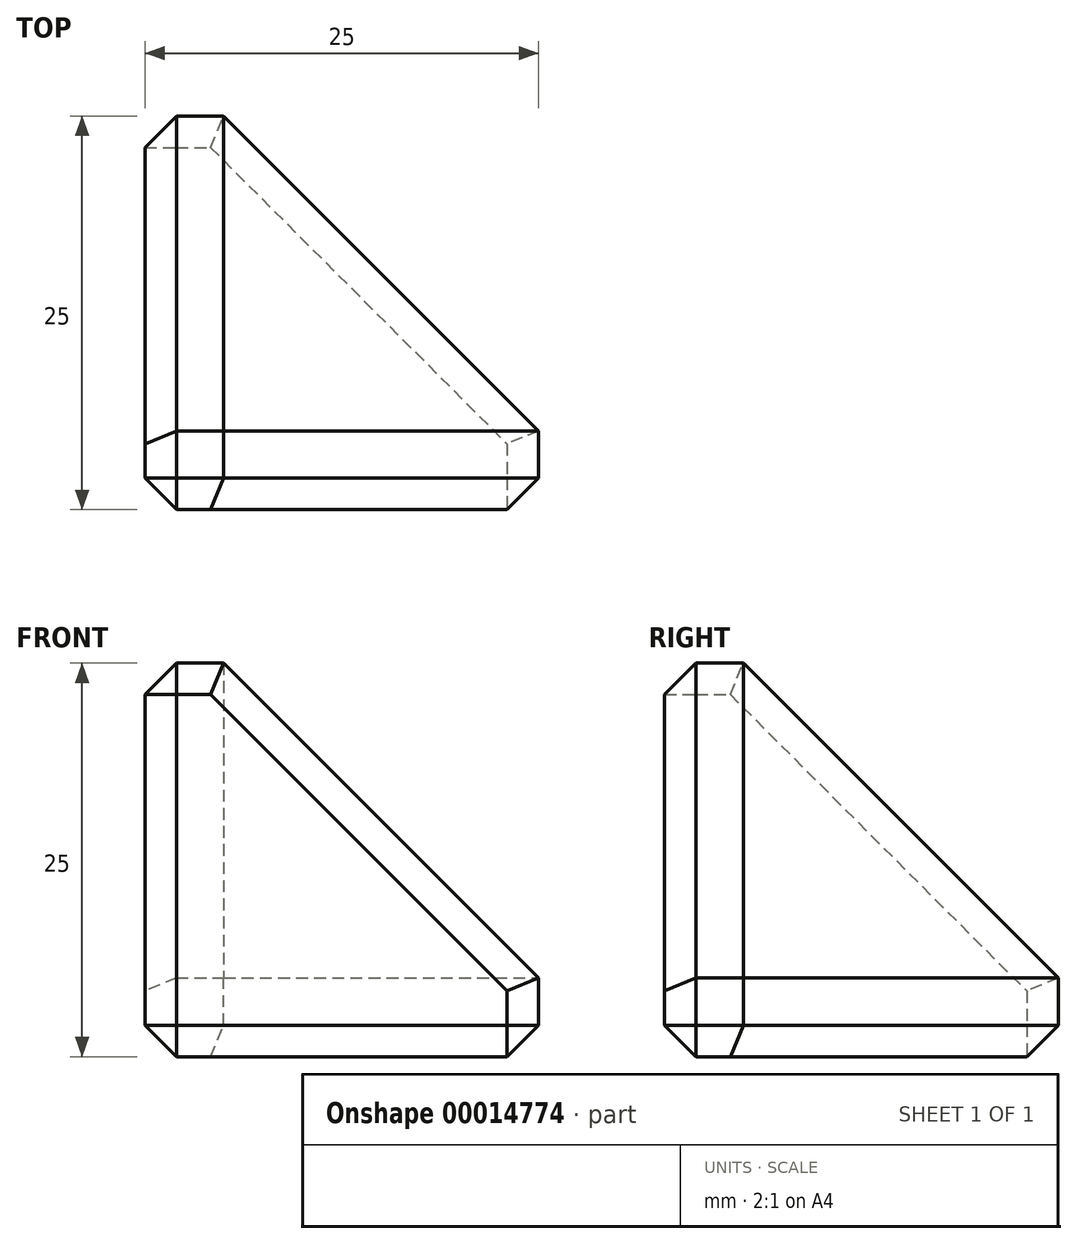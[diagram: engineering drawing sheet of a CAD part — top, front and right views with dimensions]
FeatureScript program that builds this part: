
annotation { "Feature Type Name" : "Feature", "Feature Type Description" : "" }
export const myFeature = defineFeature(function(context is Context, id is Id, definition is map)
    precondition{}
    {
        {
            var Q0;
            Q0=qCreatedBy(makeId("Top.planeOp"),FACE);
            var sketch = newSketch(context, id + "F0", { "sketchPlane" : qUnion([Q0])});
            skLineSegment(sketch, "E0.bottom", {"start": v(-12.87, 14.16) * mm, "end": v(12.13, 14.16) * mm});
            skLineSegment(sketch, "E0.top", {"start": v(-12.87, -10.84) * mm, "end": v(12.13, -10.84) * mm});
            skLineSegment(sketch, "E0.left", {"start": v(-12.87, 14.16) * mm, "end": v(-12.87, -10.84) * mm});
            skLineSegment(sketch, "E0.right", {"start": v(12.13, 14.16) * mm, "end": v(12.13, -10.84) * mm});
            skSolve(sketch);
        }
        {
            var Q0;
            Q0=makeQuery(id+"F0.imprint","IMPRINT",FACE,{"disambiguationData":[TD([[makeQuery(id+"F0.imprint","IMPRINT",EDGE,{"derivedFrom":sQuery(id+"F0.wireOp",EDGE,"E0.bottom")}),-1.0]])]});
            extrude(context, id + "F1", {"entities" : qUnion([Q0]), "depth" : 25 * mm});
        }
        {
            var Q0;
            Q0=makeQuery(id+"F1.opExtrude","CAP_FACE",FACE,{"disambiguationData":[OSD([sQuery(id+"F0.wireOp",EDGE,"E0.bottom"),sQuery(id+"F0.wireOp",EDGE,"E0.top"),sQuery(id+"F0.wireOp",EDGE,"E0.left"),sQuery(id+"F0.wireOp",EDGE,"E0.right")])],"isStart":false});
            var sketch = newSketch(context, id + "F2", { "sketchPlane" : qUnion([Q0])});
            skLineSegment(sketch, "E1", {"start": v(-7.87, 14.16) * mm, "end": v(-7.87, -5.84) * mm});
            skLineSegment(sketch, "E2", {"start": v(-7.87, -5.84) * mm, "end": v(12.13, -5.84) * mm});
            skLineSegment(sketch, "E3", {"start": v(12.13, -5.84) * mm, "end": v(12.13, 14.16) * mm});
            skLineSegment(sketch, "E4", {"start": v(12.13, 14.16) * mm, "end": v(-7.87, 14.16) * mm});
            skSolve(sketch);
        }
        {
            var Q0;
            Q0=makeQuery(id+"F2.imprint","IMPRINT",FACE,{"disambiguationData":[TD([[makeQuery(id+"F2.imprint","IMPRINT",EDGE,{"derivedFrom":sQuery(id+"F2.wireOp",EDGE,"E1")}),1.0]])]});
            extrude(context, id + "F3", {"entities" : qUnion([Q0]), "operationType" : NewBodyOperationType.REMOVE, "oppositeDirection" : true, "depth" : 20 * mm});
        }
        {
            var Q0;
            Q0=makeQuery(id+"F1.opExtrude","SWEPT_EDGE",EDGE,{"disambiguationData":[OSD([sQuery(id+"F0.wireOp",EDGE,"E0.top"),sQuery(id+"F0.wireOp",EDGE,"E0.left")])]});
            var Q1;
            Q1=makeQuery(id+"F1.opExtrude","CAP_EDGE",EDGE,{"disambiguationData":[OSD([sQuery(id+"F0.wireOp",EDGE,"E0.left")])],"isStart":false});
            var Q2;
            Q2=makeQuery(id+"F1.opExtrude","CAP_EDGE",EDGE,{"disambiguationData":[OSD([sQuery(id+"F0.wireOp",EDGE,"E0.top")])],"isStart":false});
            var Q3;
            Q3=makeQuery(id+"F1.opExtrude","SWEPT_EDGE",EDGE,{"disambiguationData":[OSD([sQuery(id+"F0.wireOp",EDGE,"E0.top"),sQuery(id+"F0.wireOp",EDGE,"E0.right")])]});
            var Q4;
            Q4=makeQuery(id+"F1.opExtrude","CAP_EDGE",EDGE,{"disambiguationData":[OSD([sQuery(id+"F0.wireOp",EDGE,"E0.top")])],"isStart":true});
            var Q5;
            Q5=makeQuery(id+"F1.opExtrude","CAP_EDGE",EDGE,{"disambiguationData":[OSD([sQuery(id+"F0.wireOp",EDGE,"E0.right")])],"isStart":true});
            var Q6;
            Q6=makeQuery(id+"F1.opExtrude","CAP_EDGE",EDGE,{"disambiguationData":[OSD([sQuery(id+"F0.wireOp",EDGE,"E0.bottom")])],"isStart":true});
            var Q7;
            Q7=makeQuery(id+"F1.opExtrude","SWEPT_EDGE",EDGE,{"disambiguationData":[OSD([sQuery(id+"F0.wireOp",EDGE,"E0.bottom"),sQuery(id+"F0.wireOp",EDGE,"E0.left")])]});
            var Q8;
            Q8=makeQuery(id+"F1.opExtrude","CAP_EDGE",EDGE,{"disambiguationData":[OSD([sQuery(id+"F0.wireOp",EDGE,"E0.left")])],"isStart":true});
            var Q9;
            Q9=makeQuery(id+"F1.opExtrude","CAP_EDGE",EDGE,{"disambiguationData":[OSD([sQuery(id+"F0.wireOp",EDGE,"E0.right")])],"isStart":false});
            var Q10;
            Q10=makeQuery(id+"F1.opExtrude","SWEPT_EDGE",EDGE,{"disambiguationData":[OSD([sQuery(id+"F0.wireOp",EDGE,"E0.bottom"),sQuery(id+"F0.wireOp",EDGE,"E0.right")])]});
            var Q11;
            Q11=makeQuery(id+"F1.opExtrude","CAP_EDGE",EDGE,{"disambiguationData":[OSD([sQuery(id+"F0.wireOp",EDGE,"E0.bottom")])],"isStart":false});
            chamfer(context, id + "F4", {"entities" : qUnion([Q0, Q1, Q2, Q3, Q4, Q5, Q6, Q7, Q8, Q9, Q10, Q11]), "width" : 2 * mm, "tangentPropagation" : true});
        }
        {
            var Q0;
            Q0=makeQuery(id+"F3.boolean.opBoolean","COPY",FACE,{"derivedFrom":makeQuery(id+"F3.opExtrude","SWEPT_FACE",FACE,{"disambiguationData":[OSD([sQuery(id+"F2.wireOp",EDGE,"E2")])]})});
            var sketch = newSketch(context, id + "F5", { "sketchPlane" : qUnion([Q0])});
            skLineSegment(sketch, "E5", {"start": v(-12.13, 5) * mm, "end": v(7.87, 25) * mm});
            skLineSegment(sketch, "E6", {"start": v(7.87, 25) * mm, "end": v(-12.13, 25) * mm});
            skLineSegment(sketch, "E7", {"start": v(-12.13, 25) * mm, "end": v(-12.13, 5) * mm});
            skSolve(sketch);
        }
        {
            var Q0;
            {var subQ0=sQuery(id+"F5.wireOp",EDGE,"E5");Q0=makeQuery(id+"F5.imprint","IMPRINT",FACE,{"disambiguationData":[TD([[makeQuery(id+"F5.imprint","IMPRINT",EDGE,{"derivedFrom":subQ0}),1.0]])]});}
            extrude(context, id + "F6", {"entities" : qUnion([Q0]), "operationType" : NewBodyOperationType.REMOVE, "oppositeDirection" : true, "depth" : 25 * mm});
        }
        {
            var Q0;
            Q0=makeQuery(id+"F3.boolean.opBoolean","COPY",FACE,{"derivedFrom":makeQuery(id+"F3.opExtrude","SWEPT_FACE",FACE,{"disambiguationData":[OSD([sQuery(id+"F2.wireOp",EDGE,"E1")])]})});
            var sketch = newSketch(context, id + "F7", { "sketchPlane" : qUnion([Q0])});
            skLineSegment(sketch, "E8", {"start": v(-5.84, 25) * mm, "end": v(14.16, 5) * mm});
            skLineSegment(sketch, "E9", {"start": v(14.16, 5) * mm, "end": v(14.16, 25) * mm});
            skPoint(sketch, "E9.endSnap0", {"position": v(14.16, 14) * mm});
            skLineSegment(sketch, "E10", {"start": v(14.16, 25) * mm, "end": v(-5.84, 25) * mm});
            skSolve(sketch);
        }
        {
            var Q0;
            {var subQ0=sQuery(id+"F7.wireOp",EDGE,"E8");Q0=makeQuery(id+"F7.imprint","IMPRINT",FACE,{"disambiguationData":[TD([[makeQuery(id+"F7.imprint","IMPRINT",EDGE,{"derivedFrom":subQ0}),1.0]])]});}
            extrude(context, id + "F8", {"entities" : qUnion([Q0]), "operationType" : NewBodyOperationType.REMOVE, "oppositeDirection" : true, "depth" : 25 * mm});
        }
        {
            var Q0;
            Q0=makeQuery(id+"F3.boolean.opBoolean","COPY",FACE,{"derivedFrom":makeQuery(id+"F3.opExtrude","CAP_FACE",FACE,{"disambiguationData":[OSD([sQuery(id+"F2.wireOp",EDGE,"E1"),sQuery(id+"F2.wireOp",EDGE,"E2"),sQuery(id+"F2.wireOp",EDGE,"E3"),sQuery(id+"F2.wireOp",EDGE,"E4")])],"isStart":false})});
            var sketch = newSketch(context, id + "F9", { "sketchPlane" : qUnion([Q0])});
            skLineSegment(sketch, "E11", {"start": v(-7.87, 14.16) * mm, "end": v(12.13, -5.84) * mm});
            skLineSegment(sketch, "E12", {"start": v(12.13, -5.84) * mm, "end": v(12.13, 14.16) * mm});
            skLineSegment(sketch, "E13", {"start": v(12.13, 14.16) * mm, "end": v(-7.87, 14.16) * mm});
            skSolve(sketch);
        }
        {
            var Q0;
            {var subQ0=sQuery(id+"F9.wireOp",EDGE,"E11");Q0=makeQuery(id+"F9.imprint","IMPRINT",FACE,{"disambiguationData":[TD([[makeQuery(id+"F9.imprint","IMPRINT",EDGE,{"derivedFrom":subQ0}),1.0]])]});}
            extrude(context, id + "F10", {"entities" : qUnion([Q0]), "operationType" : NewBodyOperationType.REMOVE, "oppositeDirection" : true, "depth" : 25 * mm});
        }
        {
            var Q0;
            Q0=makeQuery(id+"F10.boolean.opBoolean","INTERSECT",EDGE,{"derivedFrom":[makeQuery(id+"F1.opExtrude","CAP_FACE",FACE,{"disambiguationData":[OSD([sQuery(id+"F0.wireOp",EDGE,"E0.bottom"),sQuery(id+"F0.wireOp",EDGE,"E0.top"),sQuery(id+"F0.wireOp",EDGE,"E0.left"),sQuery(id+"F0.wireOp",EDGE,"E0.right")])],"isStart":true}),makeQuery(id+"F10.opExtrude","SWEPT_FACE",FACE,{"disambiguationData":[OSD([sQuery(id+"F9.wireOp",EDGE,"E11")])]})]});
            var Q1;
            Q1=makeQuery(id+"F6.boolean.opBoolean","COPY",EDGE,{"derivedFrom":makeQuery(id+"F6.opExtrude","CAP_EDGE",EDGE,{"disambiguationData":[OSD([sQuery(id+"F5.wireOp",EDGE,"E5")])],"isStart":true})});
            var Q2;
            Q2=makeQuery(id+"F8.boolean.opBoolean","COPY",EDGE,{"derivedFrom":makeQuery(id+"F8.opExtrude","CAP_EDGE",EDGE,{"disambiguationData":[OSD([sQuery(id+"F7.wireOp",EDGE,"E8")])],"isStart":true})});
            chamfer(context, id + "F11", {"entities" : qUnion([Q0, Q1, Q2]), "width" : 2 * mm, "tangentPropagation" : true});
        }
        {
            var Q0;
            Q0=makeQuery(id+"F10.boolean.opBoolean","INTERSECT",EDGE,{"derivedFrom":[makeQuery(id+"F1.opExtrude","CAP_FACE",FACE,{"disambiguationData":[OSD([sQuery(id+"F0.wireOp",EDGE,"E0.bottom"),sQuery(id+"F0.wireOp",EDGE,"E0.top"),sQuery(id+"F0.wireOp",EDGE,"E0.left"),sQuery(id+"F0.wireOp",EDGE,"E0.right")])],"isStart":true}),makeQuery(id+"F10.opExtrude","SWEPT_FACE",FACE,{"disambiguationData":[OSD([sQuery(id+"F9.wireOp",EDGE,"E11")])]})]});
            var Q1;
            Q1=makeQuery(id+"F6.boolean.opBoolean","INTERSECT",EDGE,{"derivedFrom":[makeQuery(id+"F1.opExtrude","SWEPT_FACE",FACE,{"disambiguationData":[OSD([sQuery(id+"F0.wireOp",EDGE,"E0.top")])]}),makeQuery(id+"F6.opExtrude","SWEPT_FACE",FACE,{"disambiguationData":[OSD([sQuery(id+"F5.wireOp",EDGE,"E5")])]})]});
            var Q2;
            Q2=makeQuery(id+"F8.boolean.opBoolean","INTERSECT",EDGE,{"derivedFrom":[makeQuery(id+"F1.opExtrude","SWEPT_FACE",FACE,{"disambiguationData":[OSD([sQuery(id+"F0.wireOp",EDGE,"E0.left")])]}),makeQuery(id+"F8.opExtrude","SWEPT_FACE",FACE,{"disambiguationData":[OSD([sQuery(id+"F7.wireOp",EDGE,"E8")])]})]});
            chamfer(context, id + "F12", {"entities" : qUnion([Q0, Q1, Q2]), "width" : 2 * mm, "tangentPropagation" : true});
        }
    });
